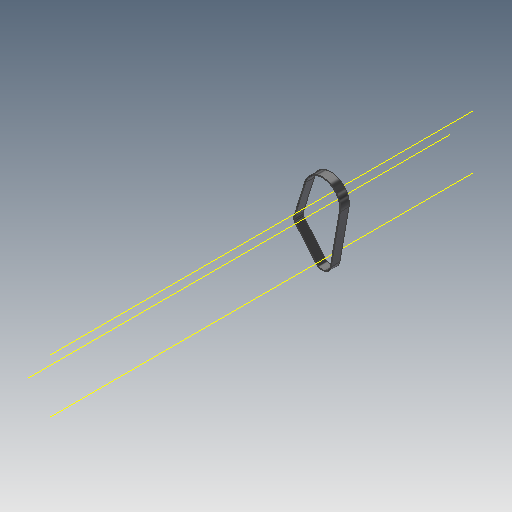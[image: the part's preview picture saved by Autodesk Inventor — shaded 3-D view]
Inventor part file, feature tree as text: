
AUTODESK INVENTOR PART (.ipt)
format: ipt  version: 2018 (Build 220112000, 112)  size: 107,008 bytes
history: native  units: mm (DEFAULTED — no unit token found)
features: other x5, plane x3, sketch x1, sweep x1
ambient origin geometry x8: Origin, YZ Plane, XZ Plane, XY Plane, X Axis, Y Axis, Z Axis, Center Point
bodies: Solid1 (feature_tree)
feature tree (10):
  sketch  "Sketch Path"  dims[d0=6.0mm d2=0.0mm d4=0.3mm d5=0.3mm d6=0.0mm d7=0.0mm d8=0.0mm d9=0.0mm d10=0.0mm d11=0.0mm d12=0.0mm d13=0.0mm]
  other  "Cross Section Plane"
  other  "Work Axis1"
  other  "Work Axis2"
  other  "Work Axis3"
  plane  "Work Plane2"
  plane  "Work Plane3"
  plane  "Work Plane4"
  sweep  "Belt"
  other  "Cross Section"
